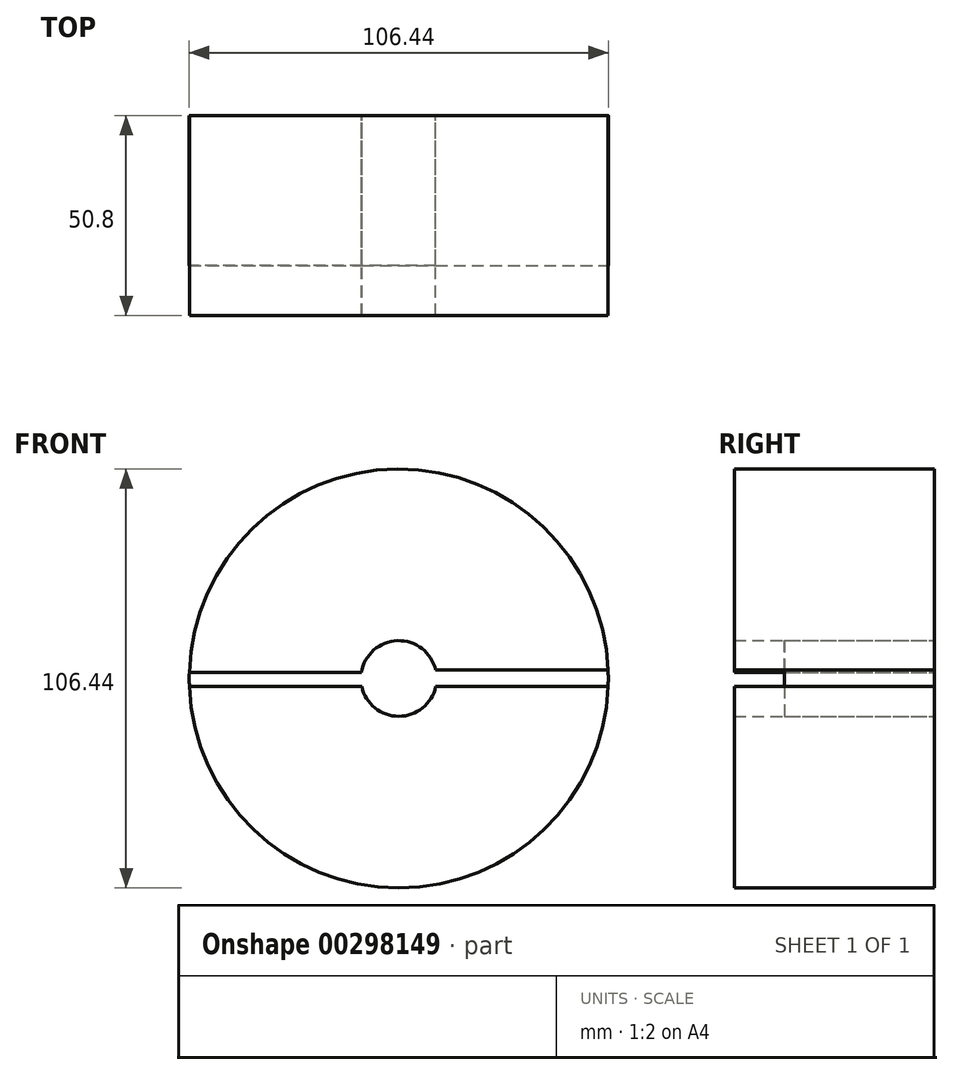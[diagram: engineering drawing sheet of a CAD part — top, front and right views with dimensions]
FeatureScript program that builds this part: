
annotation { "Feature Type Name" : "Feature", "Feature Type Description" : "" }
export const myFeature = defineFeature(function(context is Context, id is Id, definition is map)
    precondition{}
    {
        {
            var Q0;
            Q0=qCreatedBy(makeId("Front.planeOp"),FACE);
            var sketch = newSketch(context, id + "F0", { "sketchPlane" : qUnion([Q0])});
            skCircle(sketch, "E0", {"center": v(0, 0) * mm, "radius": 53.22 * mm});
            skCircle(sketch, "E1", {"center": v(0, 0) * mm, "radius": 9.6 * mm});
            skLineSegment(sketch, "E2", {"start": v(-53.2, 1.52) * mm, "end": v(-9.49, 1.52) * mm});
            skLineSegment(sketch, "E3", {"start": v(9.37, 2.11) * mm, "end": v(53.18, 2.11) * mm});
            skLineSegment(sketch, "E4", {"start": v(-9.39, -2.04) * mm, "end": v(-53.19, -2.04) * mm});
            skLineSegment(sketch, "E5", {"start": v(9.39, -2.04) * mm, "end": v(53.19, -2.04) * mm});
            skSolve(sketch);
        }
        {
            var Q0;
            {var subQ0=sQuery(id+"F0.wireOp",EDGE,"E2");Q0=makeQuery(id+"F0.imprint","IMPRINT",FACE,{"disambiguationData":[TD([[makeQuery(id+"F0.imprint","IMPRINT",EDGE,{"derivedFrom":subQ0}),1.0]])]});}
            var Q1;
            {var subQ0=sQuery(id+"F0.wireOp",EDGE,"E4");Q1=makeQuery(id+"F0.imprint","IMPRINT",FACE,{"disambiguationData":[TD([[makeQuery(id+"F0.imprint","IMPRINT",EDGE,{"derivedFrom":subQ0}),1.0]])]});}
            extrude(context, id + "F1", {"entities" : qUnion([Q0, Q1]), "depth" : 50.8 * mm});
        }
        {
            var Q0;
            {var subQ0=sQuery(id+"F0.wireOp",EDGE,"E3");Q0=makeQuery(id+"F0.imprint","IMPRINT",FACE,{"disambiguationData":[TD([[makeQuery(id+"F0.imprint","IMPRINT",EDGE,{"derivedFrom":subQ0}),-1.0]])]});}
            var Q1;
            {var subQ0=sQuery(id+"F0.wireOp",EDGE,"E1");var subQ1=makeQuery(id+"F0.imprint","INTERSECT",VERTEX,{"derivedFrom":[subQ0,sQuery(id+"F0.wireOp",EDGE,"E2")]});Q1=makeQuery(id+"F0.imprint","IMPRINT",FACE,{"disambiguationData":[TD([[makeQuery(id+"F0.imprint","IMPRINT",EDGE,{"disambiguationData":[TD([[subQ1,1.0]])],"derivedFrom":subQ0}),1.0]])]});}
            var Q2;
            {var subQ0=sQuery(id+"F0.wireOp",EDGE,"E2");Q2=makeQuery(id+"F0.imprint","IMPRINT",FACE,{"disambiguationData":[TD([[makeQuery(id+"F0.imprint","IMPRINT",EDGE,{"derivedFrom":subQ0}),-1.0]])]});}
            extrude(context, id + "F2", {"entities" : qUnion([Q0, Q1, Q2]), "depth" : 38.1 * mm});
        }
    });
